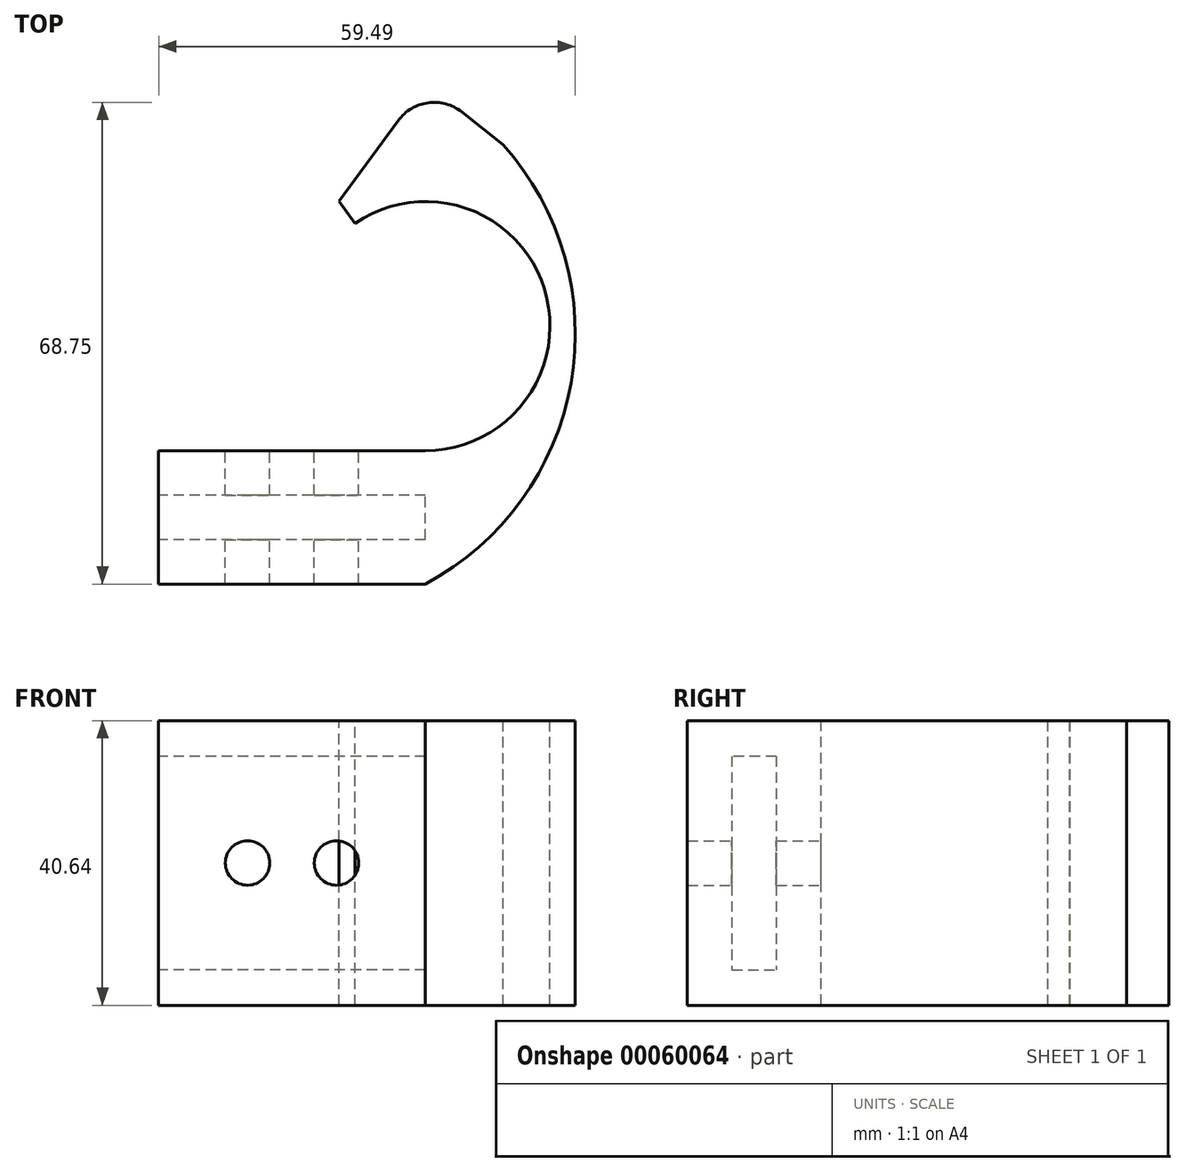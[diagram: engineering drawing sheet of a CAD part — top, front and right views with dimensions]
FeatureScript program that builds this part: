
annotation { "Feature Type Name" : "Feature", "Feature Type Description" : "" }
export const myFeature = defineFeature(function(context is Context, id is Id, definition is map)
    precondition{}
    {
        {
            var Q0;
            Q0=qCreatedBy(makeId("Top.planeOp"),FACE);
            var sketch = newSketch(context, id + "F0", { "sketchPlane" : qUnion([Q0])});
            skLineSegment(sketch, "E0.bottom", {"start": v(-77.54, 3.87) * mm, "end": v(-39.44, 3.87) * mm});
            skLineSegment(sketch, "E0.top", {"start": v(-77.54, 22.92) * mm, "end": v(-39.44, 22.92) * mm});
            skLineSegment(sketch, "E0.left", {"start": v(-77.54, 3.87) * mm, "end": v(-77.54, 22.92) * mm});
            skLineSegment(sketch, "E0.right", {"start": v(-39.44, 3.87) * mm, "end": v(-39.44, 22.92) * mm});
            skLineSegment(sketch, "E1.rect.left", {"start": v(-39.44, 10.22) * mm, "end": v(-39.44, 16.57) * mm});
            skLineSegment(sketch, "E1.rect.right", {"start": v(-77.54, 10.22) * mm, "end": v(-77.54, 16.57) * mm});
            skPoint(sketch, "E1.rect.middle", {"position": v(-58.5, 13.4) * mm});
            skPoint(sketch, "E1.rect.middle.positionSnap0", {"position": v(-39.44, 13.4) * mm});
            skPoint(sketch, "E1.rect.middle.positionSnap1", {"position": v(-58.5, 22.92) * mm});
            skPoint(sketch, "E1.rect.centerSnap0", {"position": v(-39.44, 13.4) * mm});
            skPoint(sketch, "E1.rect.centerSnap1", {"position": v(-58.5, 22.92) * mm});
            skSolve(sketch);
        }
        {
            var Q0;
            Q0 = qSketchRegion(id + "F0", true);
            extrude(context, id + "F1", {"entities" : qUnion([Q0]), "depth" : 5.08 * mm});
        }
        {
            var Q0;
            Q0=makeQuery(id+"F1.opExtrude","CAP_FACE",FACE,{"disambiguationData":[OSD([sQuery(id+"F0.wireOp",EDGE,"E0.bottom"),sQuery(id+"F0.wireOp",EDGE,"E0.top"),sQuery(id+"F0.wireOp",EDGE,"E0.left"),sQuery(id+"F0.wireOp",EDGE,"E0.right"),sQuery(id+"F0.wireOp",EDGE,"E1.rect.left"),sQuery(id+"F0.wireOp",EDGE,"E1.rect.right")])],"isStart":false});
            var sketch = newSketch(context, id + "F2", { "sketchPlane" : qUnion([Q0])});
            skLineSegment(sketch, "E2.rect.bottom", {"start": v(-39.44, 10.22) * mm, "end": v(-77.54, 10.22) * mm});
            skLineSegment(sketch, "E2.rect.top", {"start": v(-39.44, 16.57) * mm, "end": v(-77.54, 16.57) * mm});
            skLineSegment(sketch, "E2.rect.left", {"start": v(-39.44, 10.22) * mm, "end": v(-39.44, 16.57) * mm});
            skLineSegment(sketch, "E2.rect.right", {"start": v(-77.54, 10.22) * mm, "end": v(-77.54, 16.57) * mm});
            skPoint(sketch, "E2.rect.middle", {"position": v(-58.5, 13.4) * mm});
            skPoint(sketch, "E2.rect.middle.positionSnap0", {"position": v(-58.5, 22.92) * mm});
            skPoint(sketch, "E2.rect.middle.positionSnap1", {"position": v(-39.44, 13.4) * mm});
            skPoint(sketch, "E2.rect.centerSnap0", {"position": v(-58.5, 22.92) * mm});
            skPoint(sketch, "E2.rect.centerSnap1", {"position": v(-39.44, 13.4) * mm});
            skSolve(sketch);
        }
        {
            var Q0;
            {var subQ0=sQuery(id+"F2.wireOp",EDGE,"E2.rect.top");Q0=makeQuery(id+"F2.imprint","IMPRINT",FACE,{"disambiguationData":[TD([[makeQuery(id+"F2.imprint","IMPRINT",EDGE,{"derivedFrom":subQ0}),-1.0]])]});}
            var Q1;
            {var subQ0=sQuery(id+"F2.wireOp",EDGE,"E2.rect.bottom");Q1=makeQuery(id+"F2.imprint","IMPRINT",FACE,{"disambiguationData":[TD([[makeQuery(id+"F2.imprint","IMPRINT",EDGE,{"derivedFrom":subQ0}),1.0]])]});}
            extrude(context, id + "F3", {"entities" : qUnion([Q0, Q1]), "operationType" : NewBodyOperationType.ADD, "depth" : 30.48 * mm});
        }
        {
            var Q0;
            Q0=makeQuery(id+"F3.opExtrude","CAP_FACE",FACE,{"disambiguationData":[OSD([sQuery(id+"F0.wireOp",EDGE,"E0.top"),sQuery(id+"F0.wireOp",EDGE,"E0.left"),sQuery(id+"F0.wireOp",EDGE,"E0.right"),sQuery(id+"F0.wireOp",EDGE,"E1.rect.left"),sQuery(id+"F0.wireOp",EDGE,"E1.rect.right"),sQuery(id+"F2.wireOp",EDGE,"E2.rect.top")])],"isStart":false});
            var sketch = newSketch(context, id + "F4", { "sketchPlane" : qUnion([Q0])});
            skLineSegment(sketch, "E3.0.0", {"start": v(-39.44, 3.87) * mm, "end": v(-39.44, 10.22) * mm});
            skLineSegment(sketch, "E3.0.1", {"start": v(-39.44, 10.22) * mm, "end": v(-77.54, 10.22) * mm});
            skLineSegment(sketch, "E3.0.2", {"start": v(-77.54, 10.22) * mm, "end": v(-77.54, 3.87) * mm});
            skLineSegment(sketch, "E3.0.3", {"start": v(-77.54, 3.87) * mm, "end": v(-39.44, 3.87) * mm});
            skLineSegment(sketch, "E4.bottom", {"start": v(-77.54, 22.92) * mm, "end": v(-39.44, 22.92) * mm});
            skLineSegment(sketch, "E4.left", {"start": v(-77.54, 22.92) * mm, "end": v(-77.54, 3.87) * mm});
            skLineSegment(sketch, "E4.right", {"start": v(-39.44, 22.92) * mm, "end": v(-39.44, 3.87) * mm});
            skSolve(sketch);
        }
        {
            var Q0;
            Q0 = qSketchRegion(id + "F4", true);
            extrude(context, id + "F5", {"entities" : qUnion([Q0]), "operationType" : NewBodyOperationType.ADD, "depth" : 5.08 * mm});
        }
        {
            var Q0;
            Q0=makeQuery(id+"F5.opExtrude","CAP_FACE",FACE,{"disambiguationData":[OSD([sQuery(id+"F4.wireOp",EDGE,"E4.bottom"),sQuery(id+"F4.wireOp",EDGE,"E3.0.3"),sQuery(id+"F4.wireOp",EDGE,"E4.left"),sQuery(id+"F4.wireOp",EDGE,"E4.right")])],"isStart":false});
            var sketch = newSketch(context, id + "F6", { "sketchPlane" : qUnion([Q0])});
            skArc(sketch, "E5", {"start": v(-39.44, 22.92) * mm, "mid": v(-21.66, 40.7) * mm, "end": v(-39.44, 58.48) * mm});
            skArc(sketch, "E6", {"start": v(-39.44, 3.87) * mm, "mid": v(-18.67, 32.54) * mm, "end": v(-28.36, 66.6) * mm});
            skLineSegment(sketch, "E7", {"start": v(-39.44, 62.37) * mm, "end": v(-39.44, 58.48) * mm});
            skPoint(sketch, "E8.visualSharp", {"position": v(-39.44, 75.32) * mm});
            skArc(sketch, "E8.filletArc", {"start": v(-28.36, 66.6) * mm, "mid": v(-35.36, 68.3) * mm, "end": v(-39.44, 62.37) * mm});
            skArc(sketch, "E9", {"start": v(-39.44, 58.48) * mm, "mid": v(-44.72, 57.68) * mm, "end": v(-49.51, 55.35) * mm});
            skArc(sketch, "E10", {"start": v(-39.44, 62.37) * mm, "mid": v(-45.92, 61.38) * mm, "end": v(-51.8, 58.5) * mm});
            skLineSegment(sketch, "E11", {"start": v(-49.51, 55.35) * mm, "end": v(-51.8, 58.5) * mm});
            skLineSegment(sketch, "E12", {"start": v(-51.8, 58.5) * mm, "end": v(-43.33, 70.03) * mm});
            skLineSegment(sketch, "E13", {"start": v(-34.29, 71.26) * mm, "end": v(-28.36, 66.6) * mm});
            skArc(sketch, "E14.filletArc", {"start": v(-34.29, 71.26) * mm, "mid": v(-39.07, 72.56) * mm, "end": v(-43.33, 70.03) * mm});
            skSolve(sketch);
        }
        {
            var Q0;
            Q0=makeQuery(id+"F6.imprint","IMPRINT",FACE,{"disambiguationData":[TD([[makeQuery(id+"F6.imprint","IMPRINT",EDGE,{"derivedFrom":sQuery(id+"F6.wireOp",EDGE,"E5")}),-1.0]])]});
            var Q1;
            {var subQ4=sQuery(id+"F6.wireOp",EDGE,"E10");Q1=makeQuery(id+"F6.imprint","IMPRINT",FACE,{"disambiguationData":[TD([[makeQuery(id+"F6.imprint","IMPRINT",EDGE,{"derivedFrom":subQ4}),-1.0]])]});}
            var Q2;
            Q2=makeQuery(id+"F6.imprint","IMPRINT",FACE,{"disambiguationData":[TD([[makeQuery(id+"F6.imprint","IMPRINT",EDGE,{"derivedFrom":sQuery(id+"F6.wireOp",EDGE,"E7")}),-1.0]])]});
            var Q3;
            Q3=makeQuery(id+"F1.opExtrude","CAP_FACE",FACE,{"disambiguationData":[OSD([sQuery(id+"F0.wireOp",EDGE,"E0.bottom"),sQuery(id+"F0.wireOp",EDGE,"E0.top"),sQuery(id+"F0.wireOp",EDGE,"E0.left"),sQuery(id+"F0.wireOp",EDGE,"E0.right"),sQuery(id+"F0.wireOp",EDGE,"E1.rect.left"),sQuery(id+"F0.wireOp",EDGE,"E1.rect.right")])],"isStart":true});
            extrude(context, id + "F7", {"entities" : qUnion([Q0, Q1, Q2]), "operationType" : NewBodyOperationType.ADD, "endBound" : BoundingType.UP_TO_SURFACE, "oppositeDirection" : true, "endBoundEntityFace" : qUnion([Q3]), "depth" : 25.4 * mm});
        }
        {
            var Q0;
            {var subQ0=sQuery(id+"F0.wireOp",EDGE,"E0.top");Q0=makeQuery(id+"F5.boolean.opBoolean","MERGE",FACE,{"derivedFrom":[makeQuery(id+"F3.boolean.opBoolean","MERGE",FACE,{"derivedFrom":[makeQuery(id+"F1.opExtrude","SWEPT_FACE",FACE,{"disambiguationData":[OSD([subQ0])]}),makeQuery(id+"F3.opExtrude","SWEPT_FACE",FACE,{"disambiguationData":[OSD([subQ0])]})]}),makeQuery(id+"F5.opExtrude","SWEPT_FACE",FACE,{"disambiguationData":[OSD([sQuery(id+"F4.wireOp",EDGE,"E4.bottom")])]})]});}
            var sketch = newSketch(context, id + "F8", { "sketchPlane" : qUnion([Q0])});
            skCircle(sketch, "E15", {"center": v(64.84, 20.32) * mm, "radius": 3.18 * mm});
            skPoint(sketch, "E15.centerSnap0", {"position": v(77.54, 20.32) * mm});
            skCircle(sketch, "E16", {"center": v(52.14, 20.32) * mm, "radius": 3.18 * mm});
            skSolve(sketch);
        }
        {
            var Q0;
            Q0 = qSketchRegion(id + "F8", true);
            extrude(context, id + "F9", {"entities" : qUnion([Q0]), "operationType" : NewBodyOperationType.REMOVE, "oppositeDirection" : true, "depth" : 25.4 * mm});
        }
    });
